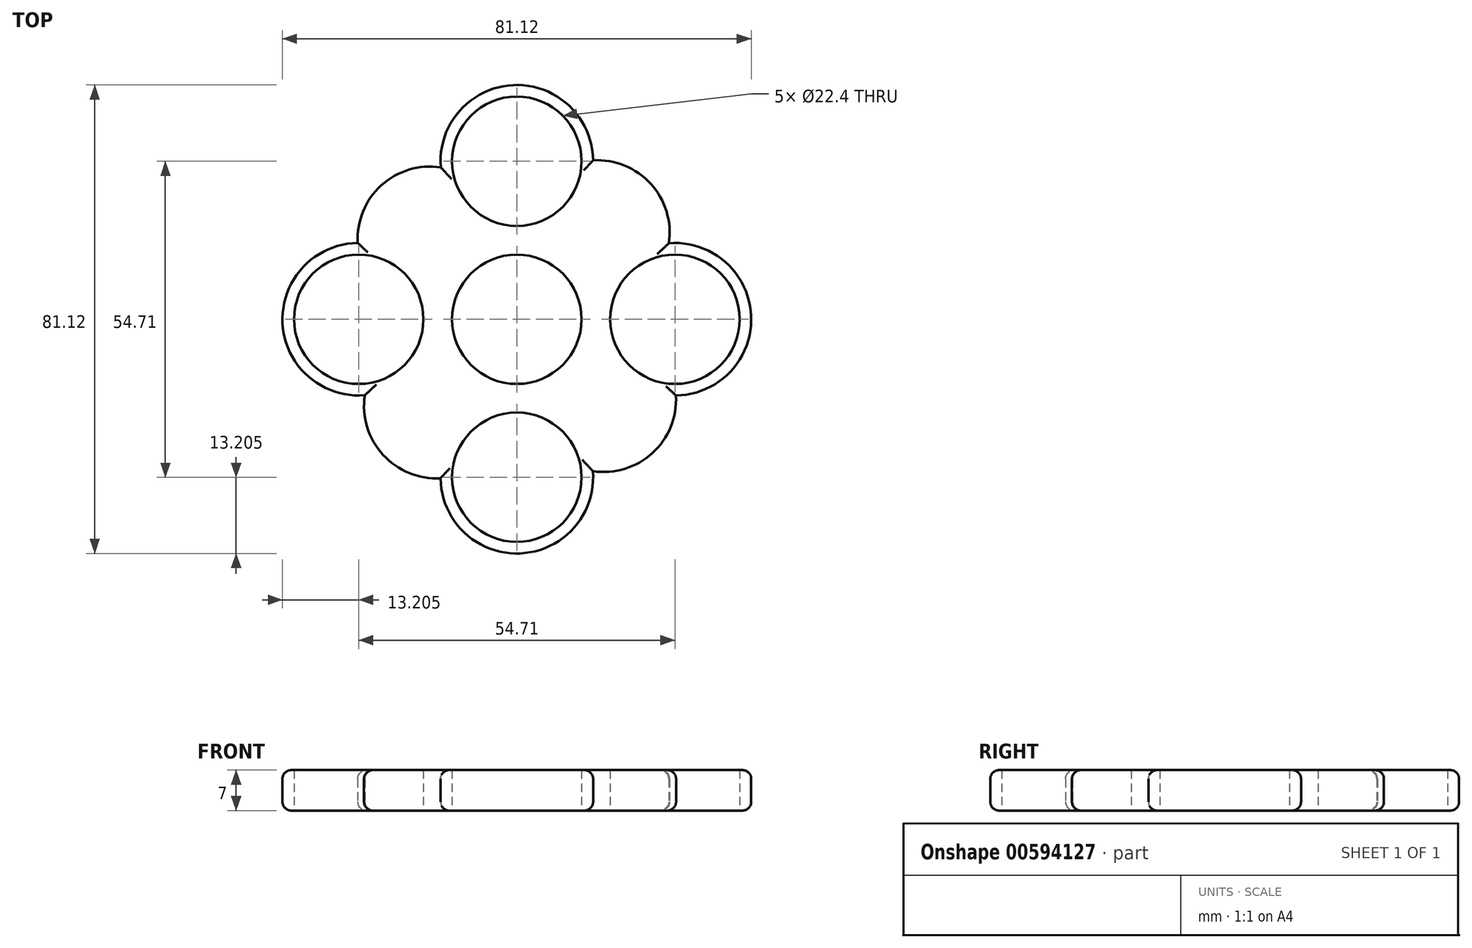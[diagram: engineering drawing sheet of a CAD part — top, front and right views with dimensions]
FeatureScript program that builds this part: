
annotation { "Feature Type Name" : "Feature", "Feature Type Description" : "" }
export const myFeature = defineFeature(function(context is Context, id is Id, definition is map)
    precondition{}
    {
        {
            var Q0;
            Q0=qCreatedBy(makeId("Top.planeOp"),FACE);
            var sketch = newSketch(context, id + "F0", { "sketchPlane" : qUnion([Q0])});
            skCircle(sketch, "E0", {"center": v(0, 0) * mm, "radius": 11.2 * mm});
            skCircle(sketch, "E1", {"center": v(0, 27.36) * mm, "radius": 11.2 * mm});
            skArc(sketch, "E2", {"start": v(13.2, 27.52) * mm, "mid": v(-0.61, 40.54) * mm, "end": v(-13.16, 26.3) * mm});
            skCircle(sketch, "E3.1.0", {"center": v(-27.36, 0) * mm, "radius": 11.2 * mm});
            skArc(sketch, "E3.1.1", {"start": v(-27.52, 13.2) * mm, "mid": v(-40.54, -0.61) * mm, "end": v(-26.3, -13.16) * mm});
            skCircle(sketch, "E3.2.0", {"center": v(0, -27.36) * mm, "radius": 11.2 * mm});
            skArc(sketch, "E3.2.1", {"start": v(-13.2, -27.52) * mm, "mid": v(0.61, -40.54) * mm, "end": v(13.16, -26.3) * mm});
            skCircle(sketch, "E3.3.0", {"center": v(27.36, 0) * mm, "radius": 11.2 * mm});
            skArc(sketch, "E3.3.1", {"start": v(27.52, -13.2) * mm, "mid": v(40.54, 0.61) * mm, "end": v(26.3, 13.16) * mm});
            skArc(sketch, "E4", {"start": v(-27.52, 13.2) * mm, "mid": v(-16.52, 20.01) * mm, "end": v(-12.26, 32.24) * mm});
            skArc(sketch, "E5.1.0", {"start": v(-13.2, -27.52) * mm, "mid": v(-20.01, -16.52) * mm, "end": v(-32.24, -12.26) * mm});
            skArc(sketch, "E5.2.0", {"start": v(27.52, -13.2) * mm, "mid": v(16.52, -20.01) * mm, "end": v(12.26, -32.24) * mm});
            skArc(sketch, "E5.3.0", {"start": v(13.2, 27.52) * mm, "mid": v(20.01, 16.52) * mm, "end": v(32.24, 12.26) * mm});
            skArc(sketch, "E6", {"start": v(26.3, 13.16) * mm, "mid": v(23.17, 23.46) * mm, "end": v(13.2, 27.52) * mm});
            skArc(sketch, "E7.1.0", {"start": v(-13.16, 26.3) * mm, "mid": v(-23.46, 23.17) * mm, "end": v(-27.52, 13.2) * mm});
            skArc(sketch, "E7.2.0", {"start": v(-26.3, -13.16) * mm, "mid": v(-23.17, -23.46) * mm, "end": v(-13.2, -27.52) * mm});
            skArc(sketch, "E7.3.0", {"start": v(13.16, -26.3) * mm, "mid": v(23.46, -23.17) * mm, "end": v(27.52, -13.2) * mm});
            skSolve(sketch);
        }
        {
            var Q0;
            Q0 = qSketchRegion(id + "F0", true);
            extrude(context, id + "F1", {"entities" : qUnion([Q0]), "depth" : 7 * mm, "offsetDistance" : 25 * mm});
        }
        {
            var Q0;
            Q0=makeQuery(id+"F1.opExtrude","CAP_EDGE",EDGE,{"disambiguationData":[OSD([sQuery(id+"F0.wireOp",EDGE,"E3.3.1")])],"isStart":false});
            var Q1;
            Q1=makeQuery(id+"F1.opExtrude","CAP_EDGE",EDGE,{"disambiguationData":[OSD([sQuery(id+"F0.wireOp",EDGE,"E7.3.0")])],"isStart":false});
            var Q2;
            Q2=makeQuery(id+"F1.opExtrude","CAP_EDGE",EDGE,{"disambiguationData":[OSD([sQuery(id+"F0.wireOp",EDGE,"E3.2.1")])],"isStart":false});
            var Q3;
            Q3=makeQuery(id+"F1.opExtrude","CAP_EDGE",EDGE,{"disambiguationData":[OSD([sQuery(id+"F0.wireOp",EDGE,"E7.2.0")])],"isStart":false});
            var Q4;
            Q4=makeQuery(id+"F1.opExtrude","CAP_EDGE",EDGE,{"disambiguationData":[OSD([sQuery(id+"F0.wireOp",EDGE,"E3.1.1")])],"isStart":false});
            var Q5;
            Q5=makeQuery(id+"F1.opExtrude","CAP_EDGE",EDGE,{"disambiguationData":[OSD([sQuery(id+"F0.wireOp",EDGE,"E7.1.0")])],"isStart":false});
            var Q6;
            Q6=makeQuery(id+"F1.opExtrude","CAP_EDGE",EDGE,{"disambiguationData":[OSD([sQuery(id+"F0.wireOp",EDGE,"E2")])],"isStart":false});
            var Q7;
            Q7=makeQuery(id+"F1.opExtrude","CAP_EDGE",EDGE,{"disambiguationData":[OSD([sQuery(id+"F0.wireOp",EDGE,"E6")])],"isStart":false});
            fillet(context, id + "F2", {"entities" : qUnion([Q0, Q1, Q2, Q3, Q4, Q5, Q6, Q7]), "radius" : 1.5 * mm, "tangentPropagation" : true, "allowEdgeOverflow" : false});
        }
        {
            var Q0;
            Q0=makeQuery(id+"F1.opExtrude","CAP_EDGE",EDGE,{"disambiguationData":[OSD([sQuery(id+"F0.wireOp",EDGE,"E3.2.1")])],"isStart":true});
            var Q1;
            Q1=makeQuery(id+"F1.opExtrude","CAP_EDGE",EDGE,{"disambiguationData":[OSD([sQuery(id+"F0.wireOp",EDGE,"E7.3.0")])],"isStart":true});
            var Q2;
            Q2=makeQuery(id+"F1.opExtrude","CAP_EDGE",EDGE,{"disambiguationData":[OSD([sQuery(id+"F0.wireOp",EDGE,"E3.3.1")])],"isStart":true});
            var Q3;
            Q3=makeQuery(id+"F1.opExtrude","CAP_EDGE",EDGE,{"disambiguationData":[OSD([sQuery(id+"F0.wireOp",EDGE,"E6")])],"isStart":true});
            var Q4;
            Q4=makeQuery(id+"F1.opExtrude","CAP_EDGE",EDGE,{"disambiguationData":[OSD([sQuery(id+"F0.wireOp",EDGE,"E2")])],"isStart":true});
            var Q5;
            Q5=makeQuery(id+"F1.opExtrude","CAP_EDGE",EDGE,{"disambiguationData":[OSD([sQuery(id+"F0.wireOp",EDGE,"E7.1.0")])],"isStart":true});
            var Q6;
            Q6=makeQuery(id+"F1.opExtrude","CAP_EDGE",EDGE,{"disambiguationData":[OSD([sQuery(id+"F0.wireOp",EDGE,"E3.1.1")])],"isStart":true});
            var Q7;
            Q7=makeQuery(id+"F1.opExtrude","CAP_EDGE",EDGE,{"disambiguationData":[OSD([sQuery(id+"F0.wireOp",EDGE,"E7.2.0")])],"isStart":true});
            fillet(context, id + "F3", {"entities" : qUnion([Q0, Q1, Q2, Q3, Q4, Q5, Q6, Q7]), "radius" : 1.5 * mm, "tangentPropagation" : true, "allowEdgeOverflow" : false});
        }
    });
